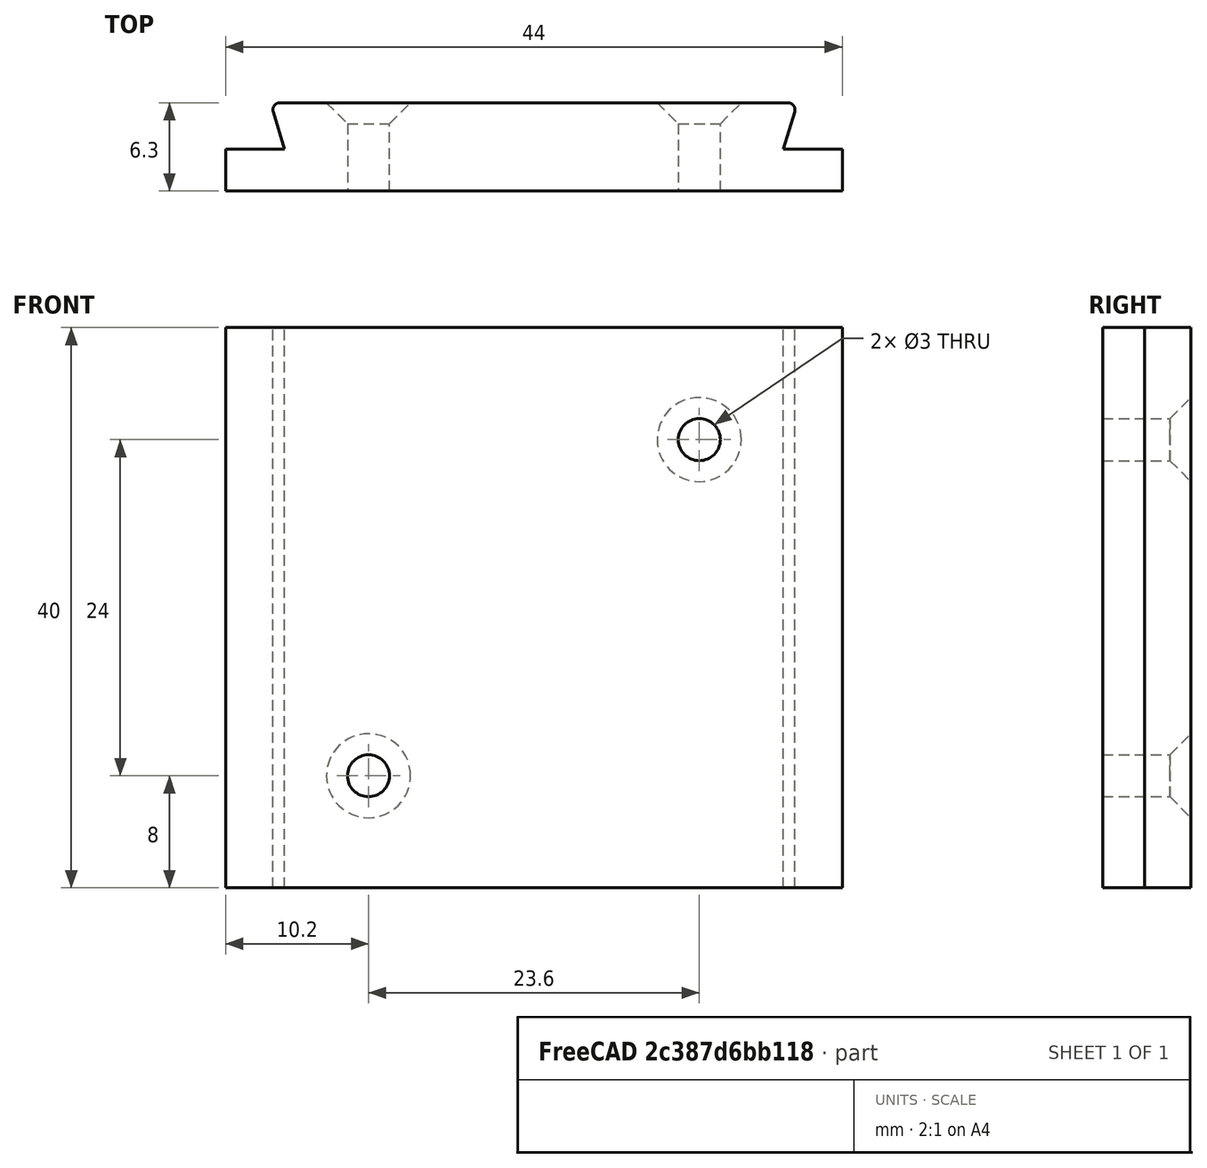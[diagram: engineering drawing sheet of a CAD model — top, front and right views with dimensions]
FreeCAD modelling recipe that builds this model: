
FCSTD DOCUMENT  (FreeCAD 0.21R33668 +26 (Git))
Label: Holder_8
License: All rights reserved
LicenseURL: http://en.wikipedia.org/wiki/All_rights_reserved
objects: Sketcher::SketchObject×2, PartDesign::Pad×1, PartDesign::Plane×1, PartDesign::Pocket×1, PartDesign::Chamfer×1, PartDesign::Fillet×1, PartDesign::Body×1, Mesh::Feature×1
note: 12 computed .brp shape members not serialized (recipe doc carries the construction recipe); baked Part::Feature solids carry a one-line shape summary decoded from their .brp

FEATURE [Sketcher::SketchObject] Sketch
  FullyConstrained = true
  MapMode = 5
  Support = -> [XY_Plane]
  sketch-geometry (8):
    g0: LineSegment StartX=4.2 StartY=3 StartZ=0 EndX=3.2 EndY=6.3 EndZ=0
    g1: LineSegment StartX=3.2 StartY=6.3 StartZ=0 EndX=40.8 EndY=6.3 EndZ=0
    g2: LineSegment StartX=40.8 StartY=6.3 StartZ=0 EndX=39.8 EndY=3 EndZ=0
    g3: LineSegment StartX=39.8 StartY=3 StartZ=0 EndX=44 EndY=3 EndZ=0
    g4: LineSegment StartX=44 StartY=3 StartZ=0 EndX=44 EndY=0 EndZ=0
    g5: LineSegment StartX=44 StartY=0 StartZ=0 EndX=0 EndY=0 EndZ=0
    g6: LineSegment StartX=0 StartY=0 StartZ=0 EndX=0 EndY=3 EndZ=0
    g7: LineSegment StartX=0 StartY=3 StartZ=0 EndX=4.2 EndY=3 EndZ=0
  constraints (24):
    c: Coincident(g0,g1)
    c: Horizontal(g1)
    c: Coincident(g1,g2)
    c: DistanceX(g1,g1) = 37.6
    c: DistanceY(g0,g0) = 3.3
    c: Coincident(g2,g3)
    c: Horizontal(g3)
    c: Coincident(g3,g4)
    c: PointOnObject(g4,g-1)
    c: Coincident(g4,g5)
    c: PointOnObject(g5,g-1)
    c: Coincident(g5,g6)
    c: Vertical(g6)
    c: Coincident(g6,g7)
    c: Coincident(g7,g0)
    c: Horizontal(g7)
    c: PointOnObject(g6,g-2)
    c: DistanceX(g0) = 3.2
    c: DistanceX(g3,g3) = 4.2
    c: Vertical(g4)
    c: DistanceX(g1,g3) = 3.2
    c: DistanceY(g3) = 3
    c: Horizontal(g0,g2)
    c: Equal(g3,g7)
FEATURE [PartDesign::Pad] Pad
  Direction = (0,0,1)
  Length = 40
  Length2 = 10
  Profile = -> Sketch
  ReferenceAxis = -> Sketch [N_Axis]
  Refine = true
  Type = 0
FEATURE [PartDesign::Plane] DatumPlane
  Length = 82.394
  MapMode = 5
  Placement = pos=(0,6.3,0) rot=(0,0.707107,0.707107;3.14159rad)
  ResizeMode = 0
  Support = -> [Pad]
  Width = 78.394
FEATURE [Sketcher::SketchObject] Sketch001
  ExternalGeometry = -> [Pad]
  FullyConstrained = true
  MapMode = 5
  Placement = pos=(0,6.3,0) rot=(0,0.707107,0.707107;3.14159rad)
  Support = -> [DatumPlane]
  sketch-geometry (2):
    g0: Circle CenterX=-33.8 CenterY=32 CenterZ=0 NormalX=0 NormalY=0 NormalZ=1 AngleXU=0 Radius=1.5
    g1: Circle CenterX=-10.2 CenterY=8 CenterZ=0 NormalX=0 NormalY=0 NormalZ=1 AngleXU=0 Radius=1.5
  constraints (6):
    c: Radius(g1) = 1.5
    c: Equal(g1,g0)
    c: DistanceX(g1,g-4) = 7
    c: DistanceY(g-4,g1) = 8
    c: DistanceY(g0,g-3) = 8
    c: DistanceX(g-3,g0) = 7
FEATURE [PartDesign::Pocket] Pocket
  BaseFeature = -> Pad
  Direction = (0,-1,2e-16)
  Length = 5
  Length2 = 5
  Profile = -> Sketch001
  ReferenceAxis = -> Sketch001 [N_Axis]
  Refine = true
  Type = 1
FEATURE [PartDesign::Chamfer] Chamfer
  Angle = 45
  Base = -> Pocket [Edge11,Edge12]
  BaseFeature = -> Pocket
  ChamferType = 0
  FlipDirection = false
  Refine = true
  Size = 1.5
  Size2 = 1
  SupportTransform = false
  UseAllEdges = false
FEATURE [PartDesign::Fillet] Fillet
  Base = -> Chamfer [Edge5,Edge2]
  BaseFeature = -> Chamfer
  Radius = 0.5
  Refine = true
  SupportTransform = false
  UseAllEdges = false
FEATURE [PartDesign::Body] Body
  Group = -> [Sketch,Pad,DatumPlane,Sketch001,Pocket,Chamfer,Fillet]
  Origin = -> Origin
  Tip = -> Fillet
FEATURE [Mesh::Feature] Mesh  label="Fillet (Meshed)"
